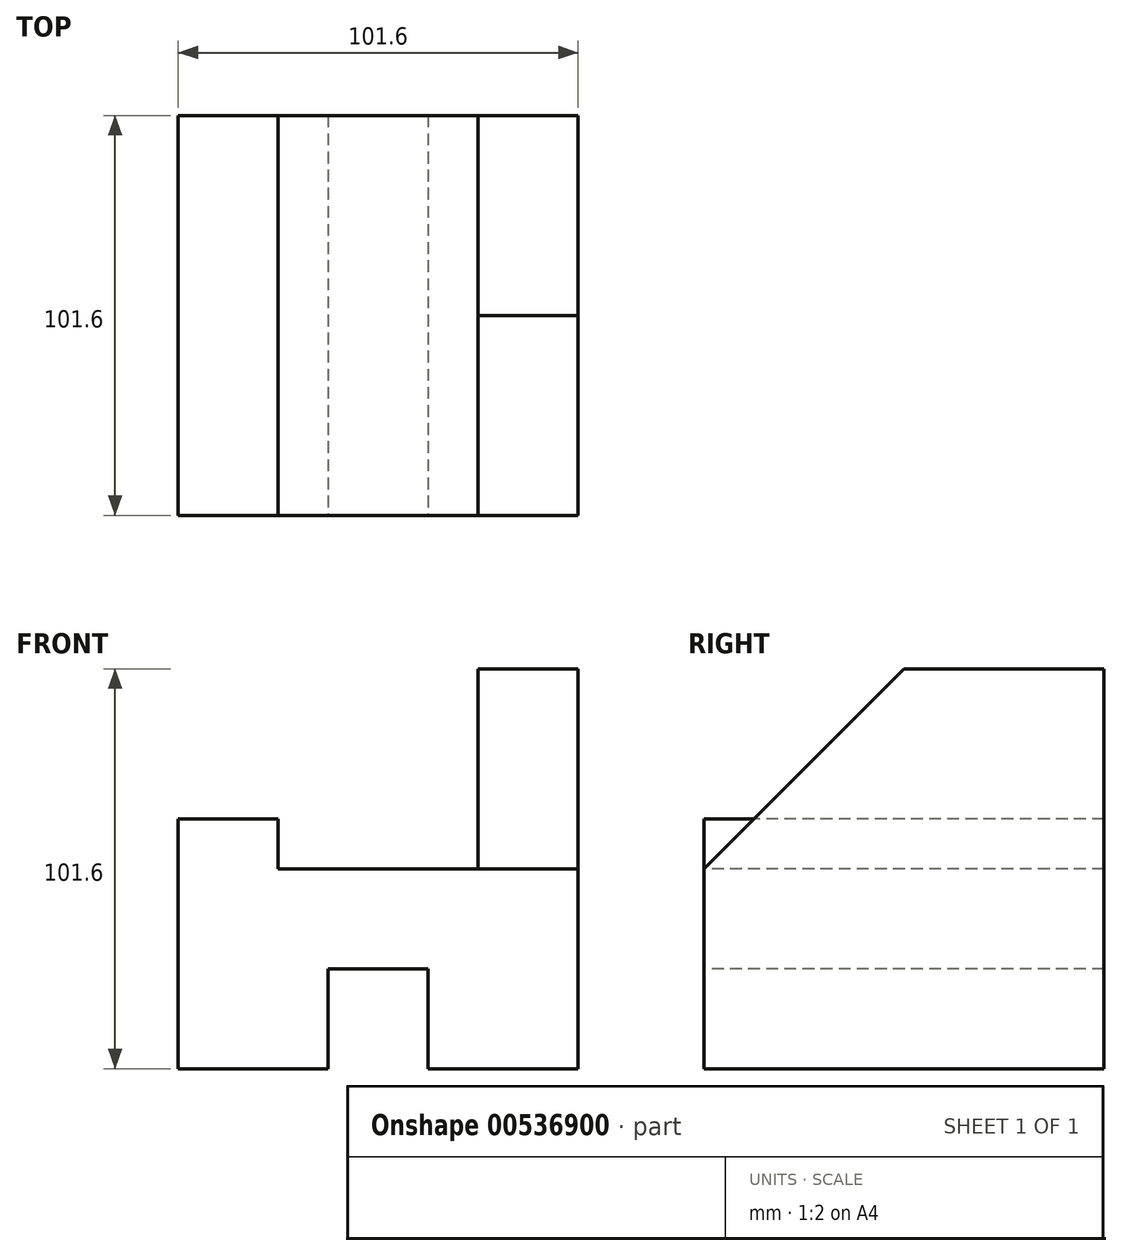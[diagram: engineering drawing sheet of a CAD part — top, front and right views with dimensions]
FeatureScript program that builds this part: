
annotation { "Feature Type Name" : "Feature", "Feature Type Description" : "" }
export const myFeature = defineFeature(function(context is Context, id is Id, definition is map)
    precondition{}
    {
        {
            var Q0;
            Q0=qCreatedBy(makeId("Front.planeOp"),FACE);
            var sketch = newSketch(context, id + "F0", { "sketchPlane" : qUnion([Q0])});
            skLineSegment(sketch, "E0.bottom", {"start": v(-39.82, -60.1) * mm, "end": v(61.78, -60.1) * mm});
            skLineSegment(sketch, "E0.top", {"start": v(-39.82, 41.5) * mm, "end": v(61.78, 41.5) * mm});
            skLineSegment(sketch, "E0.left", {"start": v(-39.82, -60.1) * mm, "end": v(-39.82, 41.5) * mm});
            skLineSegment(sketch, "E0.right", {"start": v(61.78, -60.1) * mm, "end": v(61.78, 41.5) * mm});
            skSolve(sketch);
        }
        {
            var Q0;
            Q0=makeQuery(id+"F0.imprint","IMPRINT",FACE,{"disambiguationData":[TD([[makeQuery(id+"F0.imprint","IMPRINT",EDGE,{"derivedFrom":sQuery(id+"F0.wireOp",EDGE,"E0.bottom")}),1.0]])]});
            extrude(context, id + "F1", {"entities" : qUnion([Q0]), "depth" : 101.6 * mm, "offsetDistance" : 25.4 * mm});
        }
        {
            var Q0;
            Q0=makeQuery(id+"F1.opExtrude","CAP_FACE",FACE,{"disambiguationData":[OSD([sQuery(id+"F0.wireOp",EDGE,"E0.bottom"),sQuery(id+"F0.wireOp",EDGE,"E0.top"),sQuery(id+"F0.wireOp",EDGE,"E0.left"),sQuery(id+"F0.wireOp",EDGE,"E0.right")])],"isStart":false});
            var sketch = newSketch(context, id + "F2", { "sketchPlane" : qUnion([Q0])});
            skLineSegment(sketch, "E1", {"start": v(-39.82, 3.4) * mm, "end": v(-14.42, 3.4) * mm});
            skLineSegment(sketch, "E2", {"start": v(-14.42, 3.4) * mm, "end": v(-14.42, -9.3) * mm});
            skLineSegment(sketch, "E3", {"start": v(-14.42, -9.3) * mm, "end": v(36.38, -9.3) * mm});
            skLineSegment(sketch, "E4", {"start": v(36.38, -9.3) * mm, "end": v(36.38, 41.5) * mm});
            skLineSegment(sketch, "E5", {"start": v(-1.72, -60.1) * mm, "end": v(23.68, -60.1) * mm});
            skLineSegment(sketch, "E6", {"start": v(23.68, -60.1) * mm, "end": v(61.78, -60.1) * mm});
            skSolve(sketch);
        }
        {
            var Q0;
            Q0=qSketchRegion(id+"F2",true);
            var Q1;
            {var subQ1=sQuery(id+"F2.wireOp",EDGE,"E1");Q1=makeQuery(id+"F2.imprint","IMPRINT",FACE,{"disambiguationData":[TD([[makeQuery(id+"F2.imprint","IMPRINT",EDGE,{"derivedFrom":subQ1}),1.0]])]});}
            extrude(context, id + "F3", {"entities" : qUnion([Q0, Q1]), "operationType" : NewBodyOperationType.REMOVE, "oppositeDirection" : true, "depth" : 101.6 * mm, "offsetDistance" : 25.4 * mm});
        }
        {
            var Q0;
            Q0=makeQuery(id+"F1.opExtrude","CAP_FACE",FACE,{"disambiguationData":[OSD([sQuery(id+"F0.wireOp",EDGE,"E0.bottom"),sQuery(id+"F0.wireOp",EDGE,"E0.top"),sQuery(id+"F0.wireOp",EDGE,"E0.left"),sQuery(id+"F0.wireOp",EDGE,"E0.right")])],"isStart":false});
            var sketch = newSketch(context, id + "F4", { "sketchPlane" : qUnion([Q0])});
            skLineSegment(sketch, "E7", {"start": v(-1.72, -60.1) * mm, "end": v(23.68, -60.1) * mm});
            skLineSegment(sketch, "E8", {"start": v(-1.72, -60.1) * mm, "end": v(-1.72, -34.7) * mm});
            skLineSegment(sketch, "E9", {"start": v(-1.72, -34.7) * mm, "end": v(23.68, -34.7) * mm});
            skLineSegment(sketch, "E10", {"start": v(23.68, -34.7) * mm, "end": v(23.68, -60.1) * mm});
            skSolve(sketch);
        }
        {
            var Q0;
            Q0=qSketchRegion(id+"F4",true);
            extrude(context, id + "F5", {"entities" : qUnion([Q0]), "operationType" : NewBodyOperationType.REMOVE, "oppositeDirection" : true, "depth" : 101.6 * mm, "offsetDistance" : 25.4 * mm});
        }
        {
            var Q0;
            Q0=makeQuery(id+"F1.opExtrude","SWEPT_FACE",FACE,{"disambiguationData":[OSD([sQuery(id+"F0.wireOp",EDGE,"E0.right")])]});
            var sketch = newSketch(context, id + "F6", { "sketchPlane" : qUnion([Q0])});
            skLineSegment(sketch, "E11", {"start": v(-50.8, 41.5) * mm, "end": v(-101.6, -9.3) * mm});
            skSolve(sketch);
        }
        {
            var Q0;
            {var subQ0=sQuery(id+"F6.wireOp",EDGE,"E11");Q0=makeQuery(id+"F6.imprint","IMPRINT",FACE,{"disambiguationData":[TD([[makeQuery(id+"F6.imprint","IMPRINT",EDGE,{"derivedFrom":subQ0}),-1.0]])]});}
            extrude(context, id + "F7", {"entities" : qUnion([Q0]), "operationType" : NewBodyOperationType.REMOVE, "oppositeDirection" : true, "depth" : 25.4 * mm, "offsetDistance" : 25.4 * mm});
        }
    });
